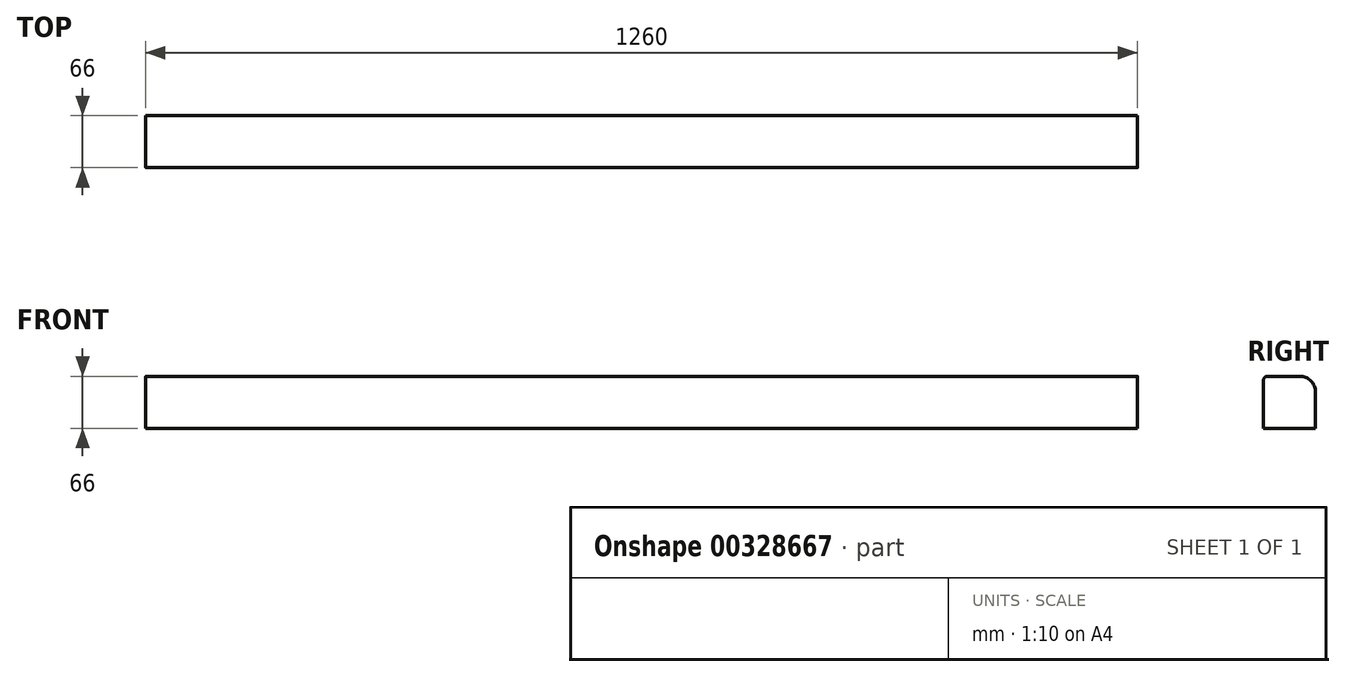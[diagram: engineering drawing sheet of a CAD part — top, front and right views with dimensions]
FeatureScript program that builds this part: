
annotation { "Feature Type Name" : "Feature", "Feature Type Description" : "" }
export const myFeature = defineFeature(function(context is Context, id is Id, definition is map)
    precondition{}
    {
        {
            var Q0;
            Q0=qCreatedBy(makeId("Right.planeOp"),FACE);
            var sketch = newSketch(context, id + "F0", { "sketchPlane" : qUnion([Q0])});
            skLineSegment(sketch, "E0.bottom", {"start": v(0, 0) * mm, "end": v(66, 0) * mm});
            skLineSegment(sketch, "E0.top", {"start": v(0, 66) * mm, "end": v(66, 66) * mm});
            skLineSegment(sketch, "E0.left", {"start": v(0, 0) * mm, "end": v(0, 66) * mm});
            skLineSegment(sketch, "E0.right", {"start": v(66, 0) * mm, "end": v(66, 66) * mm});
            skSolve(sketch);
        }
        {
            var Q0;
            Q0=qSketchRegion(id+"F0",true);
            extrude(context, id + "F1", {"entities" : qUnion([Q0]), "depth" : 1260 * mm});
        }
        {
            var Q0;
            Q0=makeQuery(id+"F1.opExtrude","SWEPT_EDGE",EDGE,{"disambiguationData":[OSD([sQuery(id+"F0.wireOp",EDGE,"E0.top"),sQuery(id+"F0.wireOp",EDGE,"E0.right")])]});
            fillet(context, id + "F2", {"entities" : qUnion([Q0]), "radius" : 20 * mm, "tangentPropagation" : true, "allowEdgeOverflow" : false});
        }
        {
            var Q0;
            Q0=makeQuery(id+"F1.opExtrude","SWEPT_EDGE",EDGE,{"disambiguationData":[OSD([sQuery(id+"F0.wireOp",EDGE,"E0.top"),sQuery(id+"F0.wireOp",EDGE,"E0.left")])]});
            fillet(context, id + "F3", {"entities" : qUnion([Q0]), "radius" : 5 * mm, "tangentPropagation" : true, "allowEdgeOverflow" : false});
        }
    });
